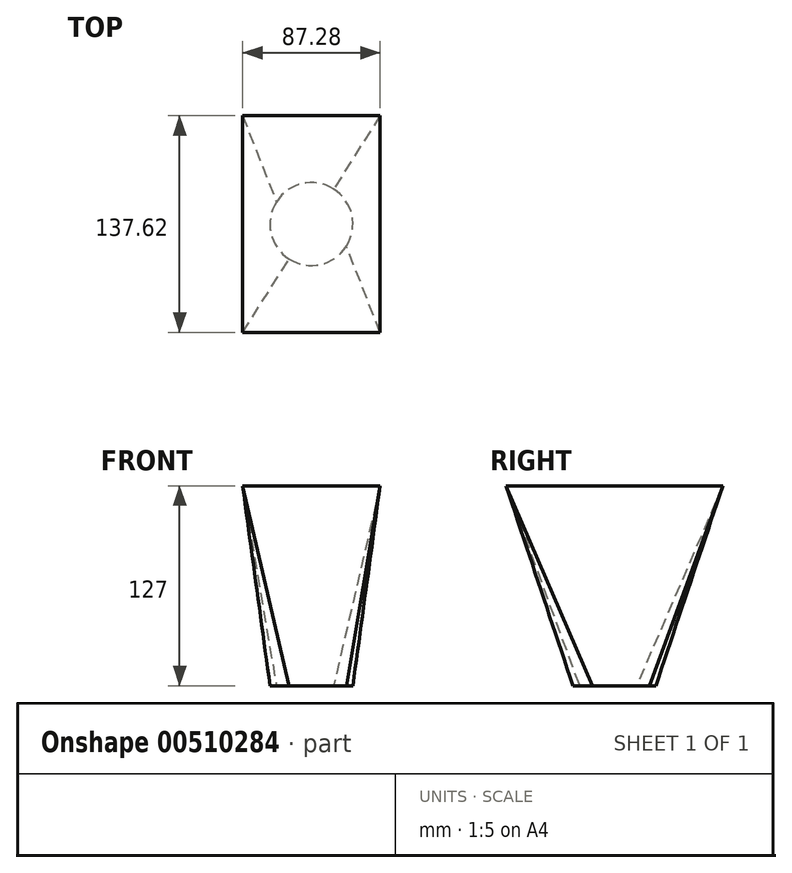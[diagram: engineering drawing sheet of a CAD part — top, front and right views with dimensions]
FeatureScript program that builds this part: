
annotation { "Feature Type Name" : "Feature", "Feature Type Description" : "" }
export const myFeature = defineFeature(function(context is Context, id is Id, definition is map)
    precondition{}
    {
        {
            var Q0;
            Q0=qCreatedBy(makeId("Top.planeOp"),FACE);
            cPlane(context, id + "F0", {"entities" : qUnion([Q0]), "cplaneType" : CPlaneType.OFFSET, "offset" : 127 * mm, "width" : 152.4 * mm, "height" : 152.4 * mm});
        }
        {
            var Q0;
            Q0=qCreatedBy(makeId("Top.planeOp"),FACE);
            var sketch = newSketch(context, id + "F1", { "sketchPlane" : qUnion([Q0])});
            skCircle(sketch, "E0", {"center": v(0, 0) * mm, "radius": 26.32 * mm});
            skSolve(sketch);
        }
        {
            var Q0;
            Q0=qCreatedBy(id+"F0.planeOp",FACE);
            var sketch = newSketch(context, id + "F2", { "sketchPlane" : qUnion([Q0])});
            skLineSegment(sketch, "E1.bottom", {"start": v(43.64, 68.8) * mm, "end": v(-43.64, 68.8) * mm});
            skLineSegment(sketch, "E1.top", {"start": v(43.64, -68.8) * mm, "end": v(-43.64, -68.8) * mm});
            skLineSegment(sketch, "E1.left", {"start": v(43.64, 68.8) * mm, "end": v(43.64, -68.8) * mm});
            skLineSegment(sketch, "E1.right", {"start": v(-43.64, 68.8) * mm, "end": v(-43.64, -68.8) * mm});
            skPoint(sketch, "E1.middle", {"position": v(0, 0) * mm});
            skLineSegment(sketch, "E2.bottom", {"start": v(107.3, 127.08) * mm, "end": v(67.85, 127.08) * mm});
            skLineSegment(sketch, "E2.top", {"start": v(107.3, 61.93) * mm, "end": v(67.85, 61.93) * mm});
            skLineSegment(sketch, "E2.left", {"start": v(107.3, 127.08) * mm, "end": v(107.3, 61.93) * mm});
            skLineSegment(sketch, "E2.right", {"start": v(67.85, 127.08) * mm, "end": v(67.85, 61.93) * mm});
            skPoint(sketch, "E2.middle", {"position": v(87.57, 94.5) * mm});
            skSolve(sketch);
        }
        {
            var Q0;
            Q0=makeQuery(id+"F2.imprint","IMPRINT",FACE,{"disambiguationData":[TD([[makeQuery(id+"F2.imprint","IMPRINT",EDGE,{"derivedFrom":sQuery(id+"F2.wireOp",EDGE,"E1.bottom")}),1.0]])]});
            var Q1;
            Q1=makeQuery(id+"F1.imprint","IMPRINT",FACE,{"disambiguationData":[TD([[makeQuery(id+"F1.imprint","IMPRINT",EDGE,{"derivedFrom":sQuery(id+"F1.wireOp",EDGE,"E0")}),1.0]])]});
            loft(context, id + "F3", {"sheetProfilesArray" : [{ "sheetProfileEntities" : qUnion([Q0]) }, { "sheetProfileEntities" : qUnion([Q1]) }]});
        }
    });
